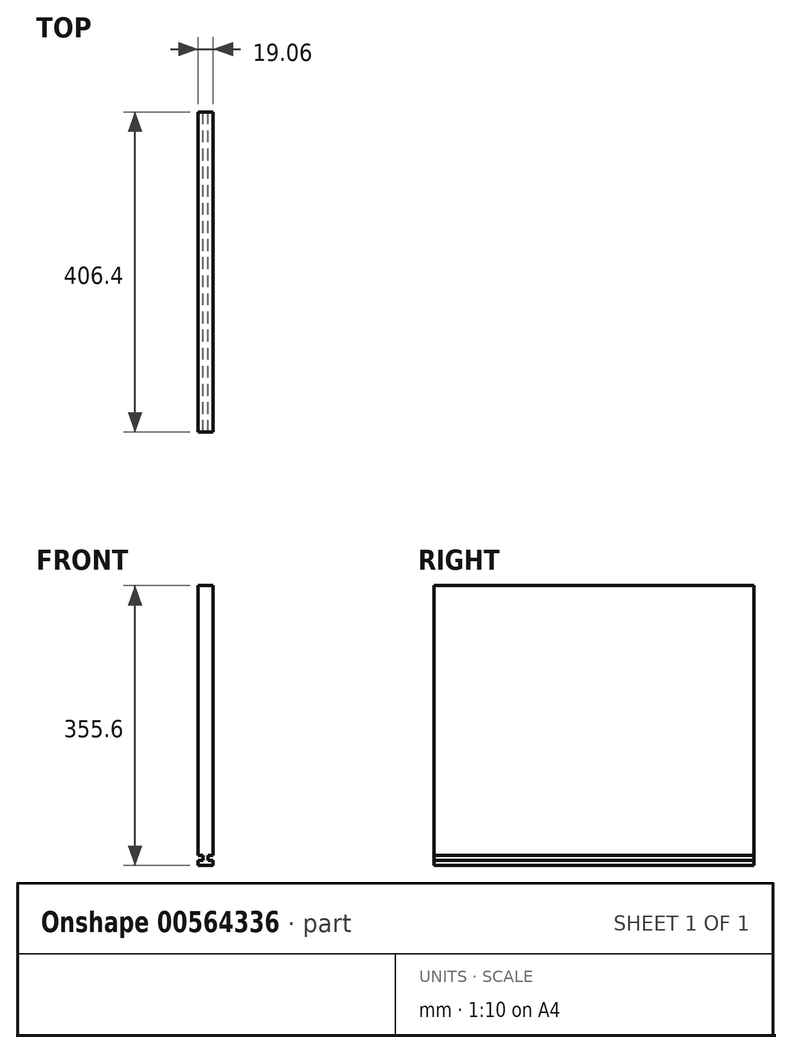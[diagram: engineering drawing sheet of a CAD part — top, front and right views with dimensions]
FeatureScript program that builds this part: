
annotation { "Feature Type Name" : "Feature", "Feature Type Description" : "" }
export const myFeature = defineFeature(function(context is Context, id is Id, definition is map)
    precondition{}
    {
        {
            var Q0;
            Q0=qCreatedBy(makeId("Right.planeOp"),FACE);
            var sketch = newSketch(context, id + "F0", { "sketchPlane" : qUnion([Q0])});
            skLineSegment(sketch, "E0.bottom", {"start": v(-203.2, 177.8) * mm, "end": v(203.2, 177.8) * mm});
            skLineSegment(sketch, "E0.top", {"start": v(-203.2, -177.8) * mm, "end": v(203.2, -177.8) * mm});
            skLineSegment(sketch, "E0.left", {"start": v(-203.2, 177.8) * mm, "end": v(-203.2, -177.8) * mm});
            skLineSegment(sketch, "E0.right", {"start": v(203.2, 177.8) * mm, "end": v(203.2, -177.8) * mm});
            skPoint(sketch, "E0.middle", {"position": v(0, 0) * mm});
            skSolve(sketch);
        }
        {
            var Q0;
            Q0=makeQuery(id+"F0.imprint","IMPRINT",FACE,{"disambiguationData":[TD([[makeQuery(id+"F0.imprint","IMPRINT",EDGE,{"derivedFrom":sQuery(id+"F0.wireOp",EDGE,"E0.bottom")}),-1.0]])]});
            extrude(context, id + "F1", {"entities" : qUnion([Q0]), "endBound" : BoundingType.SYMMETRIC, "depth" : 19.05 * mm, "offsetDistance" : 25.4 * mm});
        }
        {
            var Q0;
            Q0=qCreatedBy(makeId("Front.planeOp"),FACE);
            var sketch = newSketch(context, id + "F2", { "sketchPlane" : qUnion([Q0])});
            skLineSegment(sketch, "E1.0", {"start": v(-9.53, 177.8) * mm, "end": v(-9.53, -177.8) * mm});
            skLineSegment(sketch, "E2.0", {"start": v(9.53, 177.8) * mm, "end": v(9.53, -177.8) * mm});
            skLineSegment(sketch, "E3.bottom", {"start": v(-9.53, -171.45) * mm, "end": v(-3.18, -171.45) * mm});
            skLineSegment(sketch, "E3.top", {"start": v(-9.53, -165.1) * mm, "end": v(-3.18, -165.1) * mm});
            skLineSegment(sketch, "E3.left", {"start": v(-9.53, -171.45) * mm, "end": v(-9.53, -165.1) * mm});
            skLineSegment(sketch, "E3.right", {"start": v(-3.18, -171.45) * mm, "end": v(-3.18, -165.1) * mm});
            skLineSegment(sketch, "E4.bottom", {"start": v(9.53, -171.45) * mm, "end": v(3.18, -171.45) * mm});
            skLineSegment(sketch, "E4.top", {"start": v(9.53, -165.1) * mm, "end": v(3.17, -165.1) * mm});
            skLineSegment(sketch, "E4.left", {"start": v(9.53, -171.45) * mm, "end": v(9.53, -165.1) * mm});
            skLineSegment(sketch, "E4.right", {"start": v(3.18, -171.45) * mm, "end": v(3.17, -165.1) * mm});
            skSolve(sketch);
        }
        {
            var Q0;
            Q0 = qSketchRegion(id + "F2", true);
            extrude(context, id + "F3", {"entities" : qUnion([Q0]), "operationType" : NewBodyOperationType.REMOVE, "endBound" : BoundingType.SYMMETRIC, "depth" : 508 * mm, "offsetDistance" : 25.4 * mm});
        }
    });
